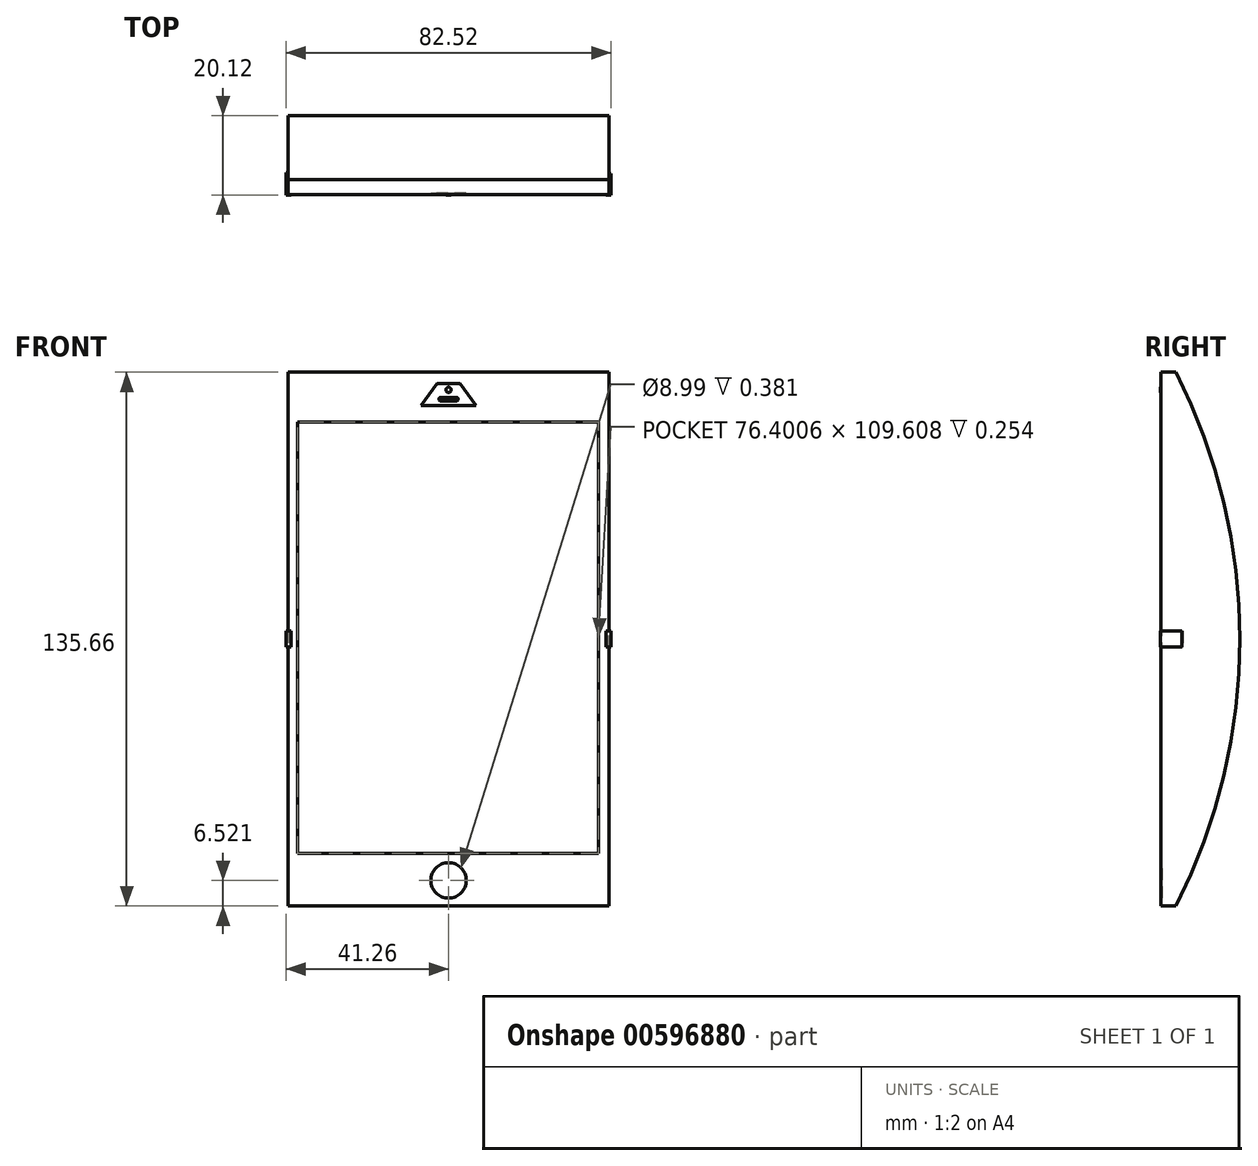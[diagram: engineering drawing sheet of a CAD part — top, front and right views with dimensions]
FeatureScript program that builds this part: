
annotation { "Feature Type Name" : "Feature", "Feature Type Description" : "" }
export const myFeature = defineFeature(function(context is Context, id is Id, definition is map)
    precondition{}
    {
        {
            var Q0;
            Q0=qCreatedBy(makeId("Front.planeOp"),FACE);
            var sketch = newSketch(context, id + "F0", { "sketchPlane" : qUnion([Q0])});
            skLineSegment(sketch, "E0", {"start": v(0, -67.53) * mm, "end": v(-40.76, -67.53) * mm});
            skLineSegment(sketch, "E1", {"start": v(-40.76, -67.53) * mm, "end": v(-40.76, 68.13) * mm});
            skLineSegment(sketch, "E2", {"start": v(-40.76, 68.13) * mm, "end": v(0, 68.13) * mm});
            skLineSegment(sketch, "E3.MirrorCS", {"start": v(40.76, 68.13) * mm, "end": v(0, 68.13) * mm});
            skLineSegment(sketch, "E4.MirrorCS", {"start": v(40.76, -67.53) * mm, "end": v(40.76, 68.13) * mm});
            skLineSegment(sketch, "E5.MirrorCS", {"start": v(0, -67.53) * mm, "end": v(40.76, -67.53) * mm});
            skSolve(sketch);
        }
        {
            var Q0;
            Q0=makeQuery(id+"F0.imprint","IMPRINT",FACE,{"disambiguationData":[TD([[makeQuery(id+"F0.imprint","IMPRINT",EDGE,{"derivedFrom":sQuery(id+"F0.wireOp",EDGE,"E0")}),-1.0]])]});
            extrude(context, id + "F1", {"entities" : qUnion([Q0]), "depth" : 3.8 * mm, "offsetDistance" : 25.4 * mm});
        }
        {
            var Q0;
            Q0=makeQuery(id+"F1.opExtrude","CAP_FACE",FACE,{"disambiguationData":[OSD([sQuery(id+"F0.wireOp",EDGE,"E0"),sQuery(id+"F0.wireOp",EDGE,"E1"),sQuery(id+"F0.wireOp",EDGE,"E2"),sQuery(id+"F0.wireOp",EDGE,"E3.MirrorCS"),sQuery(id+"F0.wireOp",EDGE,"E4.MirrorCS"),sQuery(id+"F0.wireOp",EDGE,"E5.MirrorCS")])],"isStart":false});
            var sketch = newSketch(context, id + "F2", { "sketchPlane" : qUnion([Q0])});
            skLineSegment(sketch, "E6", {"start": v(-38.35, 55.5) * mm, "end": v(38.05, 55.5) * mm});
            skLineSegment(sketch, "E7", {"start": v(38.05, 55.5) * mm, "end": v(38.05, -54.11) * mm});
            skLineSegment(sketch, "E8", {"start": v(38.05, -54.11) * mm, "end": v(-38.35, -54.11) * mm});
            skLineSegment(sketch, "E9", {"start": v(-38.35, -54.11) * mm, "end": v(-38.35, 55.5) * mm});
            skCircle(sketch, "E10", {"center": v(0, -61) * mm, "radius": 4.5 * mm});
            skSolve(sketch);
        }
        {
            var Q0;
            Q0=makeQuery(id+"F2.imprint","IMPRINT",FACE,{"disambiguationData":[TD([[makeQuery(id+"F2.imprint","IMPRINT",EDGE,{"derivedFrom":sQuery(id+"F2.wireOp",EDGE,"E6")}),-1.0]])]});
            extrude(context, id + "F3", {"entities" : qUnion([Q0]), "operationType" : NewBodyOperationType.REMOVE, "oppositeDirection" : true, "depth" : 0.25 * mm, "offsetDistance" : 25.4 * mm});
        }
        {
            var Q0;
            Q0=makeQuery(id+"F3.boolean.opBoolean","COPY",FACE,{"derivedFrom":makeQuery(id+"F3.opExtrude","CAP_FACE",FACE,{"disambiguationData":[OSD([sQuery(id+"F2.wireOp",EDGE,"E6"),sQuery(id+"F2.wireOp",EDGE,"E7"),sQuery(id+"F2.wireOp",EDGE,"E8"),sQuery(id+"F2.wireOp",EDGE,"E9")])],"isStart":false})});
            var sketch = newSketch(context, id + "F4", { "sketchPlane" : qUnion([Q0])});
            skLineSegment(sketch, "E11.0.0", {"start": v(-38.35, 55.5) * mm, "end": v(-38.35, -54.11) * mm});
            skLineSegment(sketch, "E11.0.1", {"start": v(-38.35, -54.11) * mm, "end": v(38.05, -54.11) * mm});
            skLineSegment(sketch, "E11.0.2", {"start": v(38.05, -54.11) * mm, "end": v(38.05, 55.5) * mm});
            skLineSegment(sketch, "E11.0.3", {"start": v(38.05, 55.5) * mm, "end": v(-38.35, 55.5) * mm});
            skLineSegment(sketch, "E12", {"start": v(38.05, -54.11) * mm, "end": v(-38.35, -54.11) * mm});
            skLineSegment(sketch, "E13", {"start": v(-38.35, 55.5) * mm, "end": v(38.05, 55.5) * mm});
            skSolve(sketch);
        }
        {
            var Q0;
            Q0=makeQuery(id+"F4.imprint","IMPRINT",FACE,{"disambiguationData":[TD([[makeQuery(id+"F4.imprint","IMPRINT",EDGE,{"derivedFrom":sQuery(id+"F4.wireOp",EDGE,"E11.0.0")}),-1.0]])]});
            extrude(context, id + "F5", {"entities" : qUnion([Q0]), "depth" : 0.25 * mm, "offsetDistance" : 25.4 * mm});
        }
        {
            var Q0;
            Q0=makeQuery(id+"F1.opExtrude","CAP_FACE",FACE,{"disambiguationData":[OSD([sQuery(id+"F0.wireOp",EDGE,"E0"),sQuery(id+"F0.wireOp",EDGE,"E1"),sQuery(id+"F0.wireOp",EDGE,"E2"),sQuery(id+"F0.wireOp",EDGE,"E3.MirrorCS"),sQuery(id+"F0.wireOp",EDGE,"E4.MirrorCS"),sQuery(id+"F0.wireOp",EDGE,"E5.MirrorCS")])],"isStart":false});
            var sketch = newSketch(context, id + "F6", { "sketchPlane" : qUnion([Q0])});
            skLineSegment(sketch, "E14", {"start": v(0, 65.2) * mm, "end": v(-2.98, 65.2) * mm});
            skLineSegment(sketch, "E15", {"start": v(-2.98, 65.2) * mm, "end": v(-7.01, 59.68) * mm});
            skLineSegment(sketch, "E16", {"start": v(-7.01, 59.68) * mm, "end": v(0, 59.68) * mm});
            skLineSegment(sketch, "E17.MirrorCS", {"start": v(0, 65.2) * mm, "end": v(2.98, 65.2) * mm});
            skLineSegment(sketch, "E18.MirrorCS", {"start": v(2.98, 65.2) * mm, "end": v(7.01, 59.68) * mm});
            skLineSegment(sketch, "E19.MirrorCS", {"start": v(7.01, 59.68) * mm, "end": v(0, 59.68) * mm});
            skCircle(sketch, "E20", {"center": v(0, 63.62) * mm, "radius": 0.68 * mm});
            skSolve(sketch);
        }
        {
            var Q0;
            Q0=makeQuery(id+"F6.imprint","IMPRINT",FACE,{"disambiguationData":[TD([[makeQuery(id+"F6.imprint","IMPRINT",EDGE,{"derivedFrom":sQuery(id+"F6.wireOp",EDGE,"E14")}),1.0]])]});
            extrude(context, id + "F7", {"entities" : qUnion([Q0]), "operationType" : NewBodyOperationType.REMOVE, "oppositeDirection" : true, "depth" : 0.13 * mm, "offsetDistance" : 25.4 * mm});
        }
        {
            var Q0;
            Q0=makeQuery(id+"F7.boolean.opBoolean","SPLIT",FACE,{"disambiguationData":[TD([makeQuery(id+"F7.opExtrude","SWEPT_FACE",FACE,{"disambiguationData":[OSD([sQuery(id+"F6.wireOp",EDGE,"E20")])]})])],"derivedFrom":makeQuery(id+"F1.opExtrude","CAP_FACE",FACE,{"disambiguationData":[OSD([sQuery(id+"F0.wireOp",EDGE,"E0"),sQuery(id+"F0.wireOp",EDGE,"E1"),sQuery(id+"F0.wireOp",EDGE,"E2"),sQuery(id+"F0.wireOp",EDGE,"E3.MirrorCS"),sQuery(id+"F0.wireOp",EDGE,"E4.MirrorCS"),sQuery(id+"F0.wireOp",EDGE,"E5.MirrorCS")])],"isStart":false})});
            extrude(context, id + "F8", {"entities" : qUnion([Q0]), "operationType" : NewBodyOperationType.REMOVE, "oppositeDirection" : true, "depth" : 0.13 * mm, "offsetDistance" : 25.4 * mm});
        }
        {
            var Q0;
            Q0=makeQuery(id+"F6.imprint","IMPRINT",FACE,{"disambiguationData":[TD([[makeQuery(id+"F6.imprint","IMPRINT",EDGE,{"derivedFrom":sQuery(id+"F6.wireOp",EDGE,"E20")}),1.0]])]});
            extrude(context, id + "F9", {"entities" : qUnion([Q0]), "depth" : 0.13 * mm, "offsetDistance" : 25.4 * mm});
        }
        {
            var Q0;
            Q0=makeQuery(id+"F2.imprint","IMPRINT",FACE,{"disambiguationData":[TD([[makeQuery(id+"F2.imprint","IMPRINT",EDGE,{"derivedFrom":sQuery(id+"F2.wireOp",EDGE,"E10")}),1.0]])]});
            extrude(context, id + "F10", {"entities" : qUnion([Q0]), "operationType" : NewBodyOperationType.REMOVE, "oppositeDirection" : true, "depth" : 0.38 * mm, "offsetDistance" : 25.4 * mm});
        }
        {
            var Q0;
            Q0=makeQuery(id+"F1.opExtrude","SWEPT_FACE",FACE,{"disambiguationData":[OSD([sQuery(id+"F0.wireOp",EDGE,"E4.MirrorCS")])]});
            var sketch = newSketch(context, id + "F11", { "sketchPlane" : qUnion([Q0])});
            skArc(sketch, "E21", {"start": v(0, -67.53) * mm, "mid": v(16.18, 0.3) * mm, "end": v(0, 68.13) * mm});
            skSolve(sketch);
        }
        {
            var Q0;
            Q0=makeQuery(id+"F11.imprint","IMPRINT",FACE,{"disambiguationData":[TD([[makeQuery(id+"F11.imprint","IMPRINT",EDGE,{"derivedFrom":sQuery(id+"F11.wireOp",EDGE,"E21")}),1.0]])]});
            var Q1;
            Q1=makeQuery(id+"F1.opExtrude","CAP_VERTEX",VERTEX,{"disambiguationData":[OSD([sQuery(id+"F0.wireOp",EDGE,"E1"),sQuery(id+"F0.wireOp",EDGE,"E2")])],"isStart":true});
            extrude(context, id + "F12", {"entities" : qUnion([Q0]), "endBound" : BoundingType.UP_TO_VERTEX, "oppositeDirection" : true, "depth" : 25.4 * mm, "endBoundEntityVertex" : qUnion([Q1]), "offsetDistance" : 25.4 * mm});
        }
        {
            var Q0;
            Q0=makeQuery(id+"F8.boolean.opBoolean","MERGE",FACE,{"derivedFrom":[makeQuery(id+"F7.boolean.opBoolean","COPY",FACE,{"derivedFrom":makeQuery(id+"F7.opExtrude","CAP_FACE",FACE,{"disambiguationData":[OSD([sQuery(id+"F6.wireOp",EDGE,"E14"),sQuery(id+"F6.wireOp",EDGE,"E15"),sQuery(id+"F6.wireOp",EDGE,"E16"),sQuery(id+"F6.wireOp",EDGE,"E17.MirrorCS"),sQuery(id+"F6.wireOp",EDGE,"E18.MirrorCS"),sQuery(id+"F6.wireOp",EDGE,"E19.MirrorCS"),sQuery(id+"F6.wireOp",EDGE,"E20")])],"isStart":false})}),makeQuery(id+"F8.opExtrude","CAP_FACE",FACE,{"disambiguationData":[OSD([sQuery(id+"F0.wireOp",EDGE,"E0"),sQuery(id+"F0.wireOp",EDGE,"E1"),sQuery(id+"F0.wireOp",EDGE,"E2"),sQuery(id+"F0.wireOp",EDGE,"E3.MirrorCS"),sQuery(id+"F0.wireOp",EDGE,"E4.MirrorCS"),sQuery(id+"F0.wireOp",EDGE,"E5.MirrorCS")])],"isStart":false})]});
            var sketch = newSketch(context, id + "F13", { "sketchPlane" : qUnion([Q0])});
            skLineSegment(sketch, "E22", {"start": v(0, 59.68) * mm, "end": v(0, 65.2) * mm, "construction": true});
            skLineSegment(sketch, "E23", {"start": v(0, 61.73) * mm, "end": v(-1.97, 61.73) * mm});
            skLineSegment(sketch, "E24", {"start": v(0, 60.77) * mm, "end": v(-1.97, 60.77) * mm});
            skArc(sketch, "E25", {"start": v(-1.97, 61.73) * mm, "mid": v(-2.45, 61.25) * mm, "end": v(-1.97, 60.77) * mm});
            skLineSegment(sketch, "E26.MirrorCS", {"start": v(0, 61.73) * mm, "end": v(1.97, 61.73) * mm});
            skLineSegment(sketch, "E27.MirrorCS", {"start": v(0, 60.77) * mm, "end": v(1.97, 60.77) * mm});
            skArc(sketch, "E28.MirrorCS", {"start": v(1.97, 61.73) * mm, "mid": v(2.45, 61.25) * mm, "end": v(1.97, 60.77) * mm});
            skSolve(sketch);
        }
        {
            var Q0;
            Q0=makeQuery(id+"F13.imprint","IMPRINT",FACE,{"disambiguationData":[TD([[makeQuery(id+"F13.imprint","IMPRINT",EDGE,{"derivedFrom":sQuery(id+"F13.wireOp",EDGE,"E23")}),1.0]])]});
            extrude(context, id + "F14", {"entities" : qUnion([Q0]), "operationType" : NewBodyOperationType.ADD, "depth" : 0.13 * mm, "offsetDistance" : 25.4 * mm});
        }
        {
            var Q0;
            Q0=makeQuery(id+"F1.opExtrude","SWEPT_FACE",FACE,{"disambiguationData":[OSD([sQuery(id+"F0.wireOp",EDGE,"E4.MirrorCS")])]});
            var sketch = newSketch(context, id + "F15", { "sketchPlane" : qUnion([Q0])});
            skLineSegment(sketch, "E29", {"start": v(-4.04, 0.3) * mm, "end": v(1.55, 0.3) * mm, "construction": true});
            skPoint(sketch, "E29.startSnap0", {"position": v(0, 0.3) * mm});
            skLineSegment(sketch, "E30", {"start": v(1.55, 0.3) * mm, "end": v(1.55, 2.33) * mm});
            skLineSegment(sketch, "E31", {"start": v(1.55, 2.33) * mm, "end": v(-4.04, 2.33) * mm});
            skLineSegment(sketch, "E32", {"start": v(-4.04, 2.33) * mm, "end": v(-4.04, 0.3) * mm});
            skLineSegment(sketch, "E33.MirrorCS", {"start": v(1.55, 0.3) * mm, "end": v(1.55, -1.73) * mm});
            skLineSegment(sketch, "E34.MirrorCS", {"start": v(1.55, -1.73) * mm, "end": v(-4.04, -1.73) * mm});
            skLineSegment(sketch, "E35.MirrorCS", {"start": v(-4.04, -1.73) * mm, "end": v(-4.04, 0.3) * mm});
            skSolve(sketch);
        }
        {
            var Q0;
            {var subQ0=sQuery(id+"F15.wireOp",EDGE,"E31");var subQ1=sQuery(id+"F0.wireOp",EDGE,"E4.MirrorCS");var subQ2=makeQuery(id+"F1.opExtrude","CAP_EDGE",EDGE,{"disambiguationData":[OSD([subQ1])],"isStart":true});var subQ3=makeQuery(id+"F15.imprint","INTERSECT",VERTEX,{"derivedFrom":[subQ2,subQ0]});Q0=makeQuery(id+"F15.imprint","IMPRINT",FACE,{"disambiguationData":[TD([[makeQuery(id+"F15.imprint","IMPRINT",EDGE,{"disambiguationData":[TD([[subQ3,-1.0]])],"derivedFrom":subQ0}),1.0]])]});}
            var Q1;
            {var subQ5=sQuery(id+"F15.wireOp",EDGE,"E30");Q1=makeQuery(id+"F15.imprint","IMPRINT",FACE,{"disambiguationData":[TD([[makeQuery(id+"F15.imprint","IMPRINT",EDGE,{"derivedFrom":subQ5}),1.0]])]});}
            extrude(context, id + "F16", {"entities" : qUnion([Q0, Q1]), "operationType" : NewBodyOperationType.ADD, "depth" : 0.5 * mm, "offsetDistance" : 25.4 * mm});
        }
        {
            var Q0;
            Q0=makeQuery(id+"F16.opExtrude","CAP_FACE",FACE,{"disambiguationData":[OSD([sQuery(id+"F0.wireOp",EDGE,"E4.MirrorCS"),sQuery(id+"F15.wireOp",EDGE,"E30"),sQuery(id+"F15.wireOp",EDGE,"E31"),sQuery(id+"F15.wireOp",EDGE,"E33.MirrorCS"),sQuery(id+"F15.wireOp",EDGE,"E34.MirrorCS")])],"isStart":false});
            var sketch = newSketch(context, id + "F17", { "sketchPlane" : qUnion([Q0])});
            skLineSegment(sketch, "E36", {"start": v(-3.81, -1.73) * mm, "end": v(-3.91, -1.73) * mm});
            skLineSegment(sketch, "E37", {"start": v(-3.91, -1.73) * mm, "end": v(-3.91, 2.33) * mm});
            skLineSegment(sketch, "E38", {"start": v(-3.91, 2.33) * mm, "end": v(-3.81, 2.33) * mm});
            skSolve(sketch);
        }
        {
            var Q0;
            Q0=makeQuery(id+"F17.imprint","IMPRINT",FACE,{"disambiguationData":[TD([[makeQuery(id+"F17.imprint","IMPRINT",EDGE,{"derivedFrom":sQuery(id+"F17.wireOp",EDGE,"E36")}),-1.0]])]});
            extrude(context, id + "F18", {"entities" : qUnion([Q0]), "operationType" : NewBodyOperationType.ADD, "oppositeDirection" : true, "depth" : 1.27 * mm, "offsetDistance" : 25.4 * mm});
        }
        {
            var Q0;
            Q0=makeQuery(id+"F1.opExtrude","SWEPT_FACE",FACE,{"disambiguationData":[OSD([sQuery(id+"F0.wireOp",EDGE,"E1")])]});
            var sketch = newSketch(context, id + "F19", { "sketchPlane" : qUnion([Q0])});
            skLineSegment(sketch, "E39", {"start": v(3.81, 0.3) * mm, "end": v(3.81, 2.33) * mm});
            skLineSegment(sketch, "E40", {"start": v(3.81, 2.33) * mm, "end": v(-1.78, 2.33) * mm});
            skLineSegment(sketch, "E41", {"start": v(-1.78, 2.33) * mm, "end": v(-1.78, 0.3) * mm});
            skLineSegment(sketch, "E42.MirrorCS", {"start": v(3.81, 0.3) * mm, "end": v(3.81, -1.73) * mm});
            skLineSegment(sketch, "E43.MirrorCS", {"start": v(3.81, -1.73) * mm, "end": v(-1.78, -1.73) * mm});
            skLineSegment(sketch, "E44.MirrorCS", {"start": v(-1.78, -1.73) * mm, "end": v(-1.78, 0.3) * mm});
            skSolve(sketch);
        }
        {
            var Q0;
            {var subQ4=sQuery(id+"F19.wireOp",EDGE,"E41");Q0=makeQuery(id+"F19.imprint","IMPRINT",FACE,{"disambiguationData":[TD([[makeQuery(id+"F19.imprint","IMPRINT",EDGE,{"derivedFrom":subQ4}),1.0]])]});}
            var Q1;
            {var subQ2=sQuery(id+"F19.wireOp",EDGE,"E39");Q1=makeQuery(id+"F19.imprint","IMPRINT",FACE,{"disambiguationData":[TD([[makeQuery(id+"F19.imprint","IMPRINT",EDGE,{"derivedFrom":subQ2}),1.0]])]});}
            extrude(context, id + "F20", {"entities" : qUnion([Q0, Q1]), "operationType" : NewBodyOperationType.ADD, "depth" : 0.5 * mm, "offsetDistance" : 25.4 * mm});
        }
        {
            var Q0;
            Q0=makeQuery(id+"F20.opExtrude","CAP_FACE",FACE,{"disambiguationData":[OSD([sQuery(id+"F19.wireOp",EDGE,"E39"),sQuery(id+"F19.wireOp",EDGE,"E40"),sQuery(id+"F19.wireOp",EDGE,"E41"),sQuery(id+"F19.wireOp",EDGE,"E42.MirrorCS"),sQuery(id+"F19.wireOp",EDGE,"E43.MirrorCS"),sQuery(id+"F19.wireOp",EDGE,"E44.MirrorCS")])],"isStart":false});
            var sketch = newSketch(context, id + "F21", { "sketchPlane" : qUnion([Q0])});
            skLineSegment(sketch, "E45", {"start": v(3.81, 2.33) * mm, "end": v(3.91, 2.33) * mm});
            skLineSegment(sketch, "E46", {"start": v(3.91, 2.33) * mm, "end": v(3.91, -1.73) * mm});
            skLineSegment(sketch, "E47", {"start": v(3.91, -1.73) * mm, "end": v(3.81, -1.73) * mm});
            skSolve(sketch);
        }
        {
            var Q0;
            Q0=makeQuery(id+"F21.imprint","IMPRINT",FACE,{"disambiguationData":[TD([[makeQuery(id+"F21.imprint","IMPRINT",EDGE,{"derivedFrom":sQuery(id+"F21.wireOp",EDGE,"E45")}),-1.0]])]});
            extrude(context, id + "F22", {"entities" : qUnion([Q0]), "operationType" : NewBodyOperationType.ADD, "oppositeDirection" : true, "depth" : 1.27 * mm, "offsetDistance" : 25.4 * mm});
        }
    });
